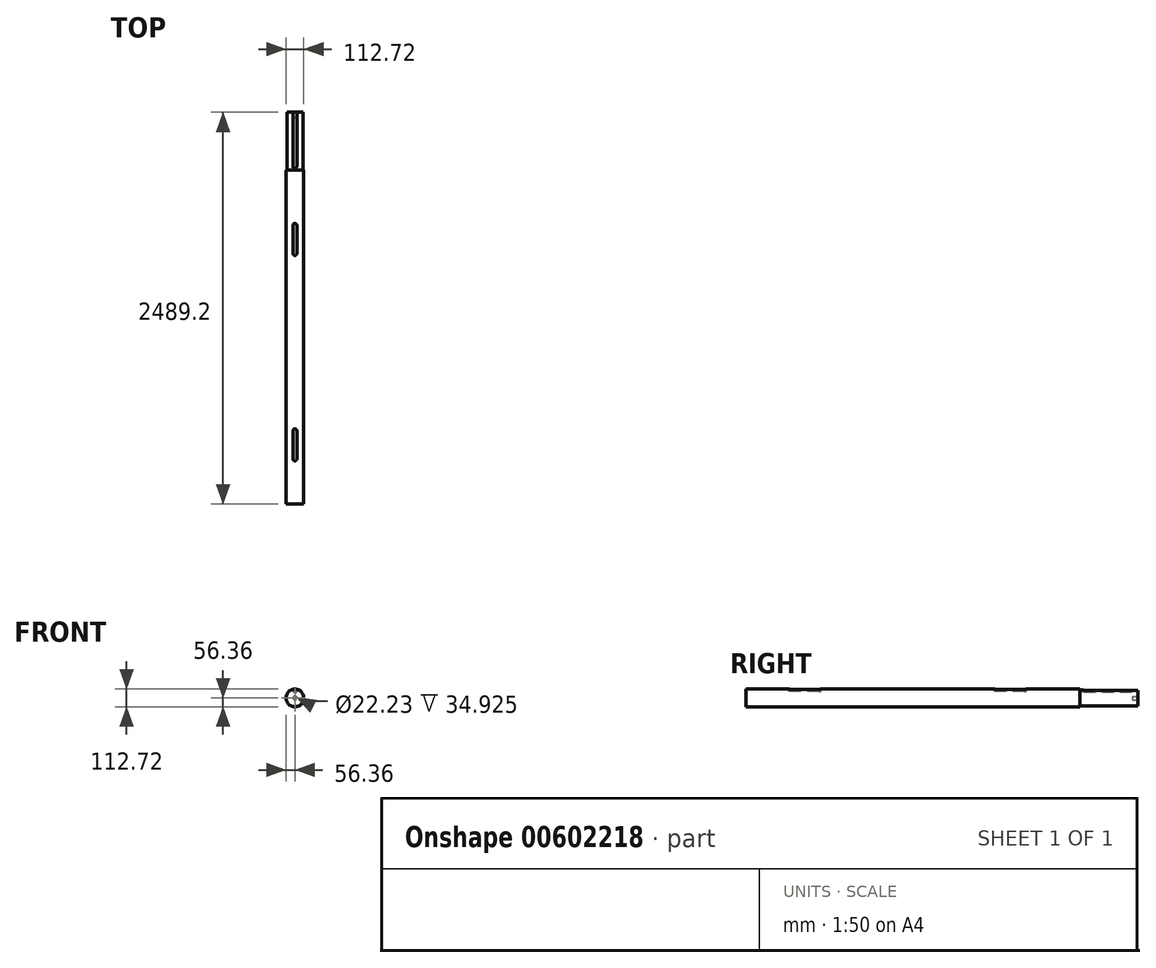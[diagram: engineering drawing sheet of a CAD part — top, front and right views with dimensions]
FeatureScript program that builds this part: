
annotation { "Feature Type Name" : "Feature", "Feature Type Description" : "" }
export const myFeature = defineFeature(function(context is Context, id is Id, definition is map)
    precondition{}
    {
        {
            var Q0;
            Q0=qCreatedBy(makeId("Front.planeOp"),FACE);
            var sketch = newSketch(context, id + "F0", { "sketchPlane" : qUnion([Q0])});
            skCircle(sketch, "E0", {"center": v(0, 0) * mm, "radius": 56.36 * mm});
            skSolve(sketch);
        }
        {
            var Q0;
            Q0 = qSketchRegion(id + "F0", true);
            extrude(context, id + "F1", {"entities" : qUnion([Q0]), "oppositeDirection" : true, "depth" : 2120.9 * mm, "offsetDistance" : 25.4 * mm});
        }
        {
            var Q0;
            Q0=makeQuery(id+"F1.opExtrude","CAP_FACE",FACE,{"disambiguationData":[OSD([sQuery(id+"F0.wireOp",EDGE,"E0")])],"isStart":false});
            var sketch = newSketch(context, id + "F2", { "sketchPlane" : qUnion([Q0])});
            skCircle(sketch, "E1", {"center": v(0, 0) * mm, "radius": 50.8 * mm});
            skSolve(sketch);
        }
        {
            var Q0;
            Q0=makeQuery(id+"F2.imprint","IMPRINT",FACE,{"disambiguationData":[TD([[makeQuery(id+"F2.imprint","IMPRINT",EDGE,{"derivedFrom":sQuery(id+"F2.wireOp",EDGE,"E1")}),1.0]])]});
            extrude(context, id + "F3", {"entities" : qUnion([Q0]), "operationType" : NewBodyOperationType.ADD, "depth" : 368.3 * mm, "offsetDistance" : 25.4 * mm});
        }
        {
            var Q0;
            Q0=makeQuery(id+"F3.opExtrude","CAP_FACE",FACE,{"disambiguationData":[OSD([sQuery(id+"F2.wireOp",EDGE,"E1")])],"isStart":false});
            var sketch = newSketch(context, id + "F4", { "sketchPlane" : qUnion([Q0])});
            skCircle(sketch, "E2", {"center": v(0, 0) * mm, "radius": 11.11 * mm});
            skSolve(sketch);
        }
        {
            var Q0;
            Q0 = qSketchRegion(id + "F4", true);
            extrude(context, id + "F5", {"entities" : qUnion([Q0]), "operationType" : NewBodyOperationType.REMOVE, "oppositeDirection" : true, "depth" : 34.92 * mm, "offsetDistance" : 25.4 * mm});
        }
        {
            var Q0;
            Q0=makeQuery(id+"F3.opExtrude","CAP_FACE",FACE,{"disambiguationData":[OSD([sQuery(id+"F2.wireOp",EDGE,"E1")])],"isStart":false});
            var sketch = newSketch(context, id + "F6", { "sketchPlane" : qUnion([Q0])});
            skCircle(sketch, "E3.0", {"center": v(0, 0) * mm, "radius": 50.8 * mm, "construction": true});
            skLineSegment(sketch, "E4", {"start": v(0, 0) * mm, "end": v(0, 71.46) * mm, "construction": true});
            skLineSegment(sketch, "E5.bottom", {"start": v(12.7, 62.23) * mm, "end": v(-12.7, 62.23) * mm});
            skLineSegment(sketch, "E5.top", {"start": v(12.7, 36.83) * mm, "end": v(-12.7, 36.83) * mm});
            skLineSegment(sketch, "E5.left", {"start": v(12.7, 62.23) * mm, "end": v(12.7, 36.83) * mm});
            skLineSegment(sketch, "E5.right", {"start": v(-12.7, 62.23) * mm, "end": v(-12.7, 36.83) * mm});
            skSolve(sketch);
        }
        {
            var Q0;
            Q0 = qSketchRegion(id + "F6", true);
            extrude(context, id + "F7", {"entities" : qUnion([Q0]), "operationType" : NewBodyOperationType.REMOVE, "oppositeDirection" : true, "depth" : 355.6 * mm, "offsetDistance" : 25.4 * mm});
        }
        {
            var Q0;
            Q0=makeQuery(id+"F7.boolean.opBoolean","COPY",EDGE,{"derivedFrom":makeQuery(id+"F7.opExtrude","CAP_EDGE",EDGE,{"disambiguationData":[OSD([sQuery(id+"F6.wireOp",EDGE,"E5.right")])],"isStart":false})});
            var Q1;
            Q1=makeQuery(id+"F7.boolean.opBoolean","COPY",EDGE,{"derivedFrom":makeQuery(id+"F7.opExtrude","CAP_EDGE",EDGE,{"disambiguationData":[OSD([sQuery(id+"F6.wireOp",EDGE,"E5.left")])],"isStart":false})});
            fillet(context, id + "F8", {"entities" : qUnion([Q0, Q1]), "radius" : 12.7 * mm, "tangentPropagation" : true, "allowEdgeOverflow" : false});
        }
        {
            var Q0;
            Q0=qCreatedBy(makeId("Top.planeOp"),FACE);
            cPlane(context, id + "F9", {"entities" : qUnion([Q0]), "cplaneType" : CPlaneType.OFFSET, "offset" : 56.36 * mm, "width" : 152.4 * mm, "height" : 152.4 * mm});
        }
        {
            var Q0;
            Q0=qCreatedBy(id+"F9.planeOp",FACE);
            var sketch = newSketch(context, id + "F10", { "sketchPlane" : qUnion([Q0])});
            skLineSegment(sketch, "E6", {"start": v(0, 0) * mm, "end": v(-223, 0) * mm, "construction": true});
            skLineSegment(sketch, "E7", {"start": v(-223, 376.24) * mm, "end": v(161.93, 376.24) * mm, "construction": true});
            skLineSegment(sketch, "E8", {"start": v(195.31, 2760.94) * mm, "end": v(-259.12, 2760.94) * mm, "construction": true});
            skLineSegment(sketch, "E9", {"start": v(148.05, 1681.16) * mm, "end": v(-172.88, 1681.16) * mm, "construction": true});
            skLineSegment(sketch, "E10", {"start": v(-56.36, 0) * mm, "end": v(-56.36, 2122.49) * mm});
            skLineSegment(sketch, "E11", {"start": v(56.36, 2122.49) * mm, "end": v(56.36, 0) * mm});
            skLineSegment(sketch, "E12", {"start": v(-56.36, 0) * mm, "end": v(-56.36, 2122.49) * mm, "construction": true});
            skLineSegment(sketch, "E13", {"start": v(56.36, 2122.49) * mm, "end": v(56.36, 0) * mm, "construction": true});
            skLineSegment(sketch, "E14", {"start": v(0, 0) * mm, "end": v(0, 2122.49) * mm, "construction": true});
            skLineSegment(sketch, "E15.bottom", {"start": v(0, 477.84) * mm, "end": v(0, 477.84) * mm});
            skLineSegment(sketch, "E15.top", {"start": v(0, 274.64) * mm, "end": v(0, 274.64) * mm});
            skLineSegment(sketch, "E15.left", {"start": v(-12.7, 465.14) * mm, "end": v(-12.7, 287.34) * mm});
            skLineSegment(sketch, "E15.right", {"start": v(12.7, 465.14) * mm, "end": v(12.7, 287.34) * mm});
            skPoint(sketch, "E15.middle", {"position": v(0, 376.24) * mm});
            skPoint(sketch, "E16.visualSharp", {"position": v(-12.7, 274.64) * mm});
            skArc(sketch, "E16.filletArc", {"start": v(-12.7, 287.34) * mm, "mid": v(-8.98, 278.36) * mm, "end": v(0, 274.64) * mm});
            skPoint(sketch, "E17.visualSharp", {"position": v(12.7, 274.64) * mm});
            skArc(sketch, "E17.filletArc", {"start": v(0, 274.64) * mm, "mid": v(8.98, 278.36) * mm, "end": v(12.7, 287.34) * mm});
            skPoint(sketch, "E18.visualSharp", {"position": v(12.7, 477.84) * mm});
            skArc(sketch, "E18.filletArc", {"start": v(12.7, 465.14) * mm, "mid": v(8.98, 474.12) * mm, "end": v(0, 477.84) * mm});
            skPoint(sketch, "E19.visualSharp", {"position": v(-12.7, 477.84) * mm});
            skArc(sketch, "E19.filletArc", {"start": v(0, 477.84) * mm, "mid": v(-8.98, 474.12) * mm, "end": v(-12.7, 465.14) * mm});
            skLineSegment(sketch, "E20.bottom", {"start": v(0, 1782.76) * mm, "end": v(0, 1782.76) * mm});
            skLineSegment(sketch, "E20.top", {"start": v(0, 1579.56) * mm, "end": v(0, 1579.56) * mm});
            skLineSegment(sketch, "E20.left", {"start": v(-12.7, 1770.06) * mm, "end": v(-12.7, 1592.26) * mm});
            skLineSegment(sketch, "E20.right", {"start": v(12.7, 1770.06) * mm, "end": v(12.7, 1592.26) * mm});
            skPoint(sketch, "E20.middle", {"position": v(0, 1681.16) * mm});
            skPoint(sketch, "E21.visualSharp", {"position": v(-12.7, 1579.56) * mm});
            skArc(sketch, "E21.filletArc", {"start": v(-12.7, 1592.26) * mm, "mid": v(-8.98, 1583.28) * mm, "end": v(0, 1579.56) * mm});
            skPoint(sketch, "E22.visualSharp", {"position": v(-12.7, 1782.76) * mm});
            skArc(sketch, "E22.filletArc", {"start": v(0, 1782.76) * mm, "mid": v(-8.98, 1779.04) * mm, "end": v(-12.7, 1770.06) * mm});
            skPoint(sketch, "E23.visualSharp", {"position": v(12.7, 1782.76) * mm});
            skArc(sketch, "E23.filletArc", {"start": v(12.7, 1770.06) * mm, "mid": v(8.98, 1779.04) * mm, "end": v(0, 1782.76) * mm});
            skPoint(sketch, "E24.visualSharp", {"position": v(12.7, 1579.56) * mm});
            skArc(sketch, "E24.filletArc", {"start": v(0, 1579.56) * mm, "mid": v(8.98, 1583.28) * mm, "end": v(12.7, 1592.26) * mm});
            skSolve(sketch);
        }
        {
            var Q0;
            Q0 = qSketchRegion(id + "F10", true);
            extrude(context, id + "F11", {"entities" : qUnion([Q0]), "operationType" : NewBodyOperationType.REMOVE, "oppositeDirection" : true, "depth" : 13.97 * mm, "offsetDistance" : 25.4 * mm});
        }
    });
